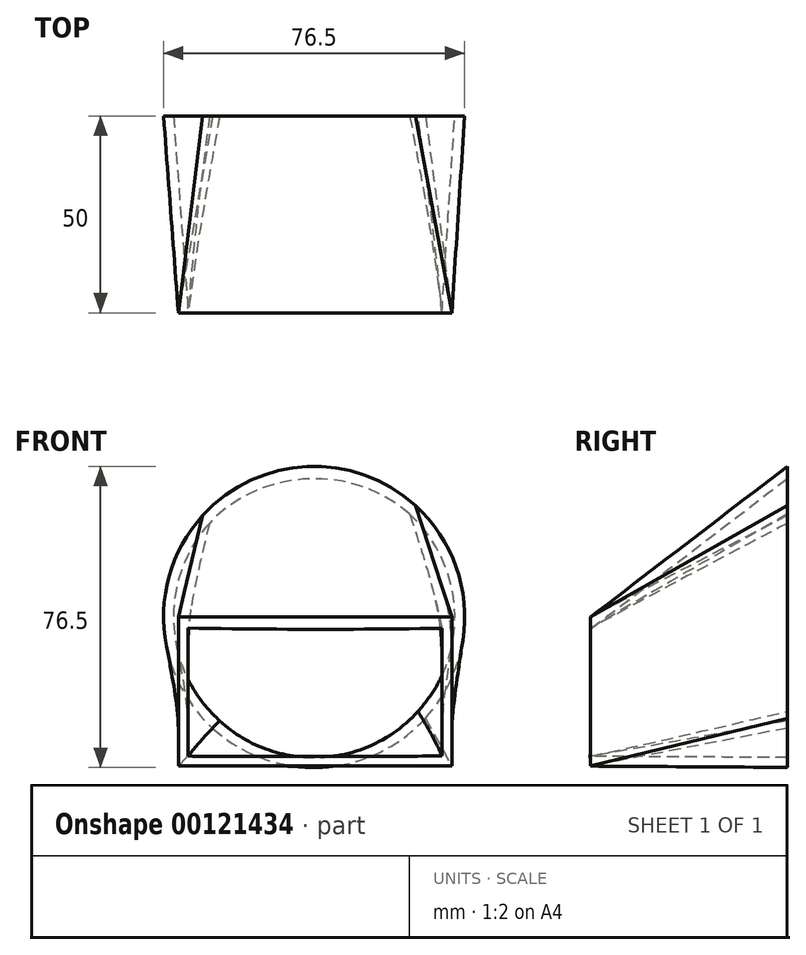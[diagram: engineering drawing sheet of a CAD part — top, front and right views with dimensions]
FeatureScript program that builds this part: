
annotation { "Feature Type Name" : "Feature", "Feature Type Description" : "" }
export const myFeature = defineFeature(function(context is Context, id is Id, definition is map)
    precondition{}
    {
        {
            var Q0;
            Q0=qCreatedBy(makeId("Front.planeOp"),FACE);
            var sketch = newSketch(context, id + "F0", { "sketchPlane" : qUnion([Q0])});
            skCircle(sketch, "E0", {"center": v(0, 0) * mm, "radius": 38.25 * mm});
            skSolve(sketch);
        }
        {
            var Q0;
            Q0=qCreatedBy(makeId("Front.planeOp"),FACE);
            cPlane(context, id + "F1", {"entities" : qUnion([Q0]), "cplaneType" : CPlaneType.OFFSET, "offset" : 50 * mm, "width" : 150 * mm, "height" : 150 * mm});
        }
        {
            var Q0;
            Q0=qCreatedBy(id+"F1.planeOp",FACE);
            var sketch = newSketch(context, id + "F2", { "sketchPlane" : qUnion([Q0])});
            skLineSegment(sketch, "E1.bottom", {"start": v(-34.5, -37.9) * mm, "end": v(34.97, -37.9) * mm});
            skLineSegment(sketch, "E1.top", {"start": v(-34.5, 0) * mm, "end": v(34.97, 0) * mm});
            skLineSegment(sketch, "E1.left", {"start": v(-34.5, -37.9) * mm, "end": v(-34.5, 0) * mm});
            skLineSegment(sketch, "E1.right", {"start": v(34.97, -37.9) * mm, "end": v(34.97, 0) * mm});
            skSolve(sketch);
        }
        {
            var Q0;
            Q0=makeQuery(id+"F0.imprint","IMPRINT",FACE,{"disambiguationData":[TD([[makeQuery(id+"F0.imprint","IMPRINT",EDGE,{"derivedFrom":sQuery(id+"F0.wireOp",EDGE,"E0")}),1.0]])]});
            var Q1;
            Q1=makeQuery(id+"F2.imprint","IMPRINT",FACE,{"disambiguationData":[TD([[makeQuery(id+"F2.imprint","IMPRINT",EDGE,{"derivedFrom":sQuery(id+"F2.wireOp",EDGE,"E1.bottom")}),1.0]])]});
            loft(context, id + "F3", {"sheetProfilesArray" : [{ "sheetProfileEntities" : qUnion([Q0]) }, { "sheetProfileEntities" : qUnion([Q1]) }]});
        }
        {
            var Q0;
            Q0=makeQuery(id+"F3.opLoft","CAP_FACE",FACE,{"disambiguationData":[OSD([makeQuery(id+"F2.imprint","IMPRINT",FACE,{"disambiguationData":[TD([[makeQuery(id+"F2.imprint","IMPRINT",EDGE,{"derivedFrom":sQuery(id+"F2.wireOp",EDGE,"E1.bottom")}),1.0]])]})])],"isStart":true});
            var Q1;
            Q1=makeQuery(id+"F3.opLoft","CAP_FACE",FACE,{"disambiguationData":[OSD([makeQuery(id+"F0.imprint","IMPRINT",FACE,{"disambiguationData":[TD([[makeQuery(id+"F0.imprint","IMPRINT",EDGE,{"derivedFrom":sQuery(id+"F0.wireOp",EDGE,"E0")}),1.0]])]})])],"isStart":true});
            shell(context, id + "F4", {"entities" : qUnion([Q0, Q1]), "thickness" : 2.5 * mm});
        }
    });
